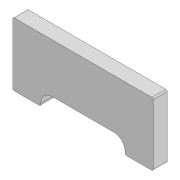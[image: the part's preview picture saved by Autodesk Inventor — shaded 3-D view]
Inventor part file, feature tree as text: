
AUTODESK INVENTOR PART (.ipt)
format: ipt  version: 2020 (Build 240168000, 168)  size: 97,792 bytes
history: native  units: mm
features: extrude x1, sketch x1
ambient origin geometry x8: Origin, YZ Plane, XZ Plane, XY Plane, X Axis, Y Axis, Z Axis, Center Point
bodies: Solid1 (feature_tree)
feature tree (2):
  extrude  "Extrusion1"  Depth=45.0mm
  sketch  "Sketch1"  dims[d0=100.0mm d1=45.0mm d2=20.0mm d3=10.0mm d4=8.0mm d5=1.0mm d6=1.0mm d7=10.0mm d8=0.0mm]
